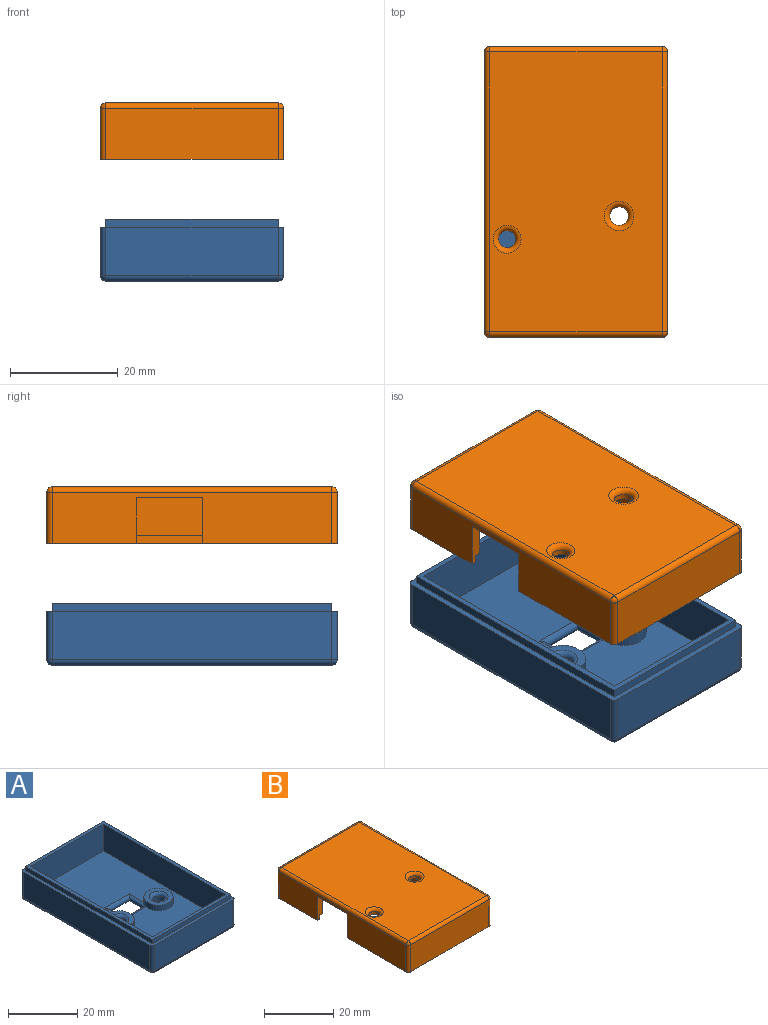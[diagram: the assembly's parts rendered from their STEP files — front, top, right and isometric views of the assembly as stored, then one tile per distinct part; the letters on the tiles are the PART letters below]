
ASSEMBLY  parts=2 mates=1
PART A: 42 faces, bbox 34x54x11.5 mm
  f0: plane 54x34mm, normal (0,0,1), area 171.1mm2, adj f9,f10,f11,f12,f13,f14,f15,f16
  f1: cylinder r=1.75mm len=3.5mm, axis (0,0,-1), area 22mm2, adj f29,f36
  f2: cylinder r=1.75mm len=3.5mm, axis (0,0,-1), area 22mm2, adj f30,f31
  f3: plane 50x30mm, normal (0,0,1), area 1309.3mm2, adj f5,f6,f7,f8,f17,f19,f32,f33
  f4: plane 52x32mm, normal (0,0,-1), area 1536.5mm2, adj f21,f24,f25,f28,f31,f32,f33,f34
  f5: plane 50x9.5mm, normal (1,0,0), area 475mm2, adj f3,f6,f8,f40
  f6: plane 30x9.5mm, normal (0,1,0), area 285mm2, adj f3,f5,f7,f40
  f7: plane 50x9.5mm, normal (-1,0,0), area 475mm2, adj f3,f6,f8,f40
  f8: plane 30x9.5mm, normal (0,-1,0), area 285mm2, adj f3,f5,f7,f40
  f9: plane 32x9mm, normal (0,1,0), area 288mm2, adj f0,f10,f16,f25
  f10: cylinder r=1mm len=9mm, axis (0,0,-1), area 14.1mm2, adj f0,f9,f11,f27
  f11: plane 52x9mm, normal (-1,0,0), area 468mm2, adj f0,f10,f12,f28
  f12: cylinder r=1mm len=9mm, axis (0,0,-1), area 14.1mm2, adj f0,f11,f13,f26
  f13: plane 32x9mm, normal (0,-1,0), area 288mm2, adj f0,f12,f14,f24
  f14: cylinder r=1mm len=9mm, axis (0,0,-1), area 14.1mm2, adj f0,f13,f15,f22
  f15: plane 52x9mm, normal (1,0,0), area 468mm2, adj f0,f14,f16,f21
  f16: cylinder r=1mm len=9mm, axis (0,0,-1), area 14.1mm2, adj f0,f9,f15,f23
  f17: cylinder r=4.25mm len=8.5mm, axis (0,0,-1), area 53.7mm2, adj f3,f18,f32,f34
  f18: plane 8.5x8.5mm, normal (0,0,1), area 33mm2, adj f17,f30
  f19: cylinder r=4.25mm len=8.5mm, axis (0,0,-1), area 53.7mm2, adj f3,f20,f32,f33
  f20: plane 8.5x8.5mm, normal (0,0,1), area 33mm2, adj f19,f29
  f21: cylinder r=1mm len=52mm, axis (0,1,0), area 81.7mm2, adj f4,f15,f22,f23
  f22: sphere r=1mm, area 1.6mm2, adj f14,f21,f24
  f23: sphere r=1mm, area 1.6mm2, adj f16,f21,f25
  f24: cylinder r=1mm len=32mm, axis (1,0,0), area 50.3mm2, adj f4,f13,f22,f26
  f25: cylinder r=1mm len=32mm, axis (-1,0,0), area 50.3mm2, adj f4,f9,f23,f27
  f26: sphere r=1mm, area 1.6mm2, adj f12,f24,f28
  f27: sphere r=1mm, area 1.6mm2, adj f10,f25,f28
  f28: cylinder r=1mm len=52mm, axis (0,-1,0), area 81.7mm2, adj f4,f11,f26,f27
  f29: torus R=2.75mm, axis (0,0,1), area 20.9mm2, adj f1,f20
  f30: torus R=2.75mm, axis (0,0,1), area 20.9mm2, adj f2,f18
  f31: torus R=2.75mm, axis (0,0,1), area 20.9mm2, adj f2,f4
  f32: cylinder r=1mm len=10mm, axis (1,0,0), area 26.4mm2, adj f3,f4,f17,f19,f33,f34
  f33: cylinder r=1mm len=8mm, axis (0,1,0), area 20.2mm2, adj f3,f4,f19,f32,f35
  f34: cylinder r=1mm len=8mm, axis (0,-1,0), area 20.2mm2, adj f3,f4,f17,f32,f35
  f35: cylinder r=1mm len=10mm, axis (-1,0,0), area 27.4mm2, adj f3,f4,f33,f34
  f36: torus R=2.75mm, axis (0,0,1), area 20.9mm2, adj f1,f4
  f37: plane 32x1.5mm, normal (0,1,0), area 48mm2, adj f0,f38,f39,f40
  f38: plane 52x1.5mm, normal (1,0,0), area 78mm2, adj f0,f37,f40,f41
  f39: plane 52x1.5mm, normal (-1,0,0), area 78mm2, adj f0,f37,f40,f41
  f40: plane 52x32mm, normal (0,0,1), area 164mm2, adj f5,f6,f7,f8,f37,f38,f39,f41
  f41: plane 32x1.5mm, normal (0,-1,0), area 48mm2, adj f0,f38,f39,f40
PART B: 36 faces, bbox 34x54x10.5 mm
  f0: plane 52x32mm, normal (0,0,-1), area 151.7mm2, adj f1,f13,f14,f15,f16,f17,f18,f19
  f1: plane 23x7mm, normal (1,0,0), area 161mm2, adj f0,f11,f13,f17
  f2: plane 32x9.5mm, normal (0,1,0), area 304mm2, adj f3,f9,f20,f30
  f3: cylinder r=1mm len=9.5mm, axis (0,0,1), area 14.9mm2, adj f2,f4,f20,f28
  f4: plane 52x9.5mm, normal (-1,0,0), area 389.5mm2, adj f3,f5,f11,f17,f18,f20,f26
  f5: cylinder r=1mm len=9.5mm, axis (0,0,1), area 14.9mm2, adj f4,f6,f20,f27
  f6: plane 32x9.5mm, normal (0,-1,0), area 304mm2, adj f5,f7,f20,f29
  f7: cylinder r=1mm len=9.5mm, axis (0,0,1), area 14.9mm2, adj f6,f8,f20,f31
  f8: plane 52x9.5mm, normal (1,0,0), area 494mm2, adj f7,f9,f20,f33
  f9: cylinder r=1mm len=9.5mm, axis (0,0,1), area 14.9mm2, adj f2,f8,f20,f32
  f10: cylinder r=1.75mm len=3.5mm, axis (0,0,1), area 11mm2, adj f11,f35
  f11: plane 50x32mm, normal (0,0,-1), area 1506.9mm2, adj f1,f4,f10,f13,f14,f15,f16,f17
  f12: plane 52x32mm, normal (0,0,1), area 1619mm2, adj f26,f29,f30,f33,f34,f35
  f13: plane 30x7mm, normal (0,1,0), area 210mm2, adj f0,f1,f11,f16
  f14: plane 14.7x7mm, normal (1,0,0), area 102.9mm2, adj f0,f11,f15,f18
  f15: plane 30x7mm, normal (0,-1,0), area 210mm2, adj f0,f11,f14,f16
  f16: plane 50x7mm, normal (-1,0,0), area 350mm2, adj f0,f11,f13,f15
  f17: plane 8.5x2mm, normal (0,1,0), area 15.5mm2, adj f0,f1,f4,f11,f19,f20
  f18: plane 8.5x2mm, normal (0,-1,0), area 15.5mm2, adj f0,f4,f11,f14,f20,f24
  f19: plane 24x1.5mm, normal (1,0,0), area 36mm2, adj f0,f17,f20,f21
  f20: plane 54x34mm, normal (0,0,-1), area 158.8mm2, adj f2,f3,f4,f5,f6,f7,f8,f9
  f21: plane 32x1.5mm, normal (0,1,0), area 48mm2, adj f0,f19,f20,f22
  f22: plane 52x1.5mm, normal (-1,0,0), area 78mm2, adj f0,f20,f21,f23
  f23: plane 32x1.5mm, normal (0,-1,0), area 48mm2, adj f0,f20,f22,f24
  f24: plane 15.7x1.5mm, normal (1,0,0), area 23.6mm2, adj f0,f18,f20,f23
  f25: cylinder r=1.6mm len=3.2mm, axis (0,0,1), area 10.1mm2, adj f11,f34
  f26: cylinder r=1mm len=52mm, axis (0,-1,0), area 81.7mm2, adj f4,f12,f27,f28
  f27: sphere r=1mm, area 1.6mm2, adj f5,f26,f29
  f28: sphere r=1mm, area 1.6mm2, adj f3,f26,f30
  f29: cylinder r=1mm len=32mm, axis (1,0,0), area 50.3mm2, adj f6,f12,f27,f31
  f30: cylinder r=1mm len=32mm, axis (-1,0,0), area 50.3mm2, adj f2,f12,f28,f32
  f31: sphere r=1mm, area 1.6mm2, adj f7,f29,f33
  f32: sphere r=1mm, area 1.6mm2, adj f9,f30,f33
  f33: cylinder r=1mm len=52mm, axis (0,1,0), area 81.7mm2, adj f8,f12,f31,f32
  f34: torus R=2.6mm, axis (0,0,1), area 19.4mm2, adj f12,f25
  f35: torus R=2.75mm, axis (0,0,1), area 20.9mm2, adj f10,f12
PLACE A t=(-2.47,-0.99,-5.1)mm fixed
PLACE B t=(-2.47,-0.99,27.99)mm
MATE slider B.f7 <-> A.f14  axis (0,0,-1) through (13.53,-26.99,18.99)mm
